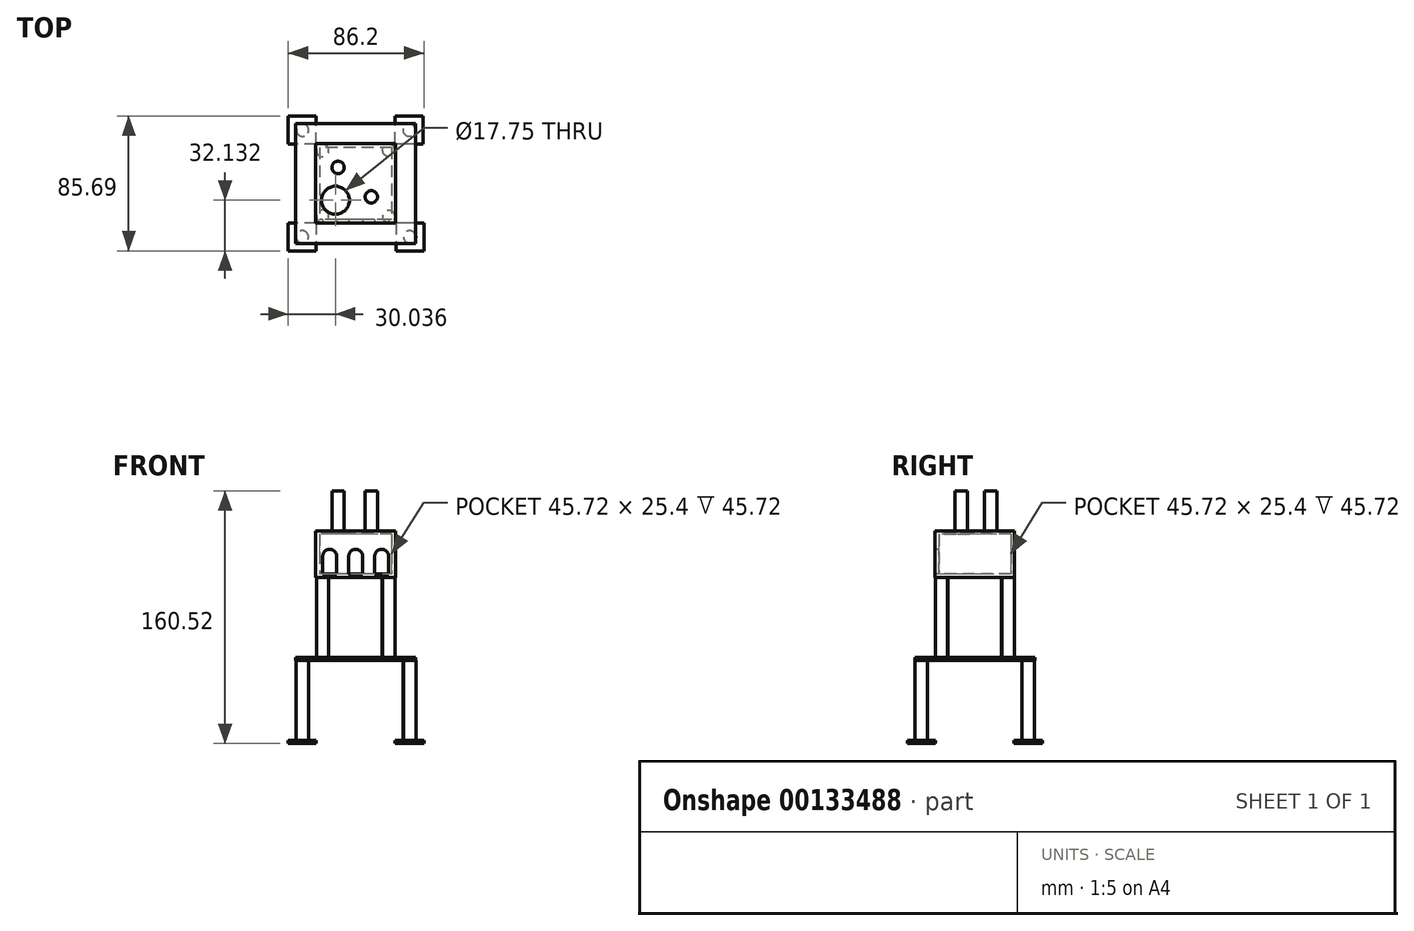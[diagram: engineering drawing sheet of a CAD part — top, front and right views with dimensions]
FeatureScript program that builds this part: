
annotation { "Feature Type Name" : "Feature", "Feature Type Description" : "" }
export const myFeature = defineFeature(function(context is Context, id is Id, definition is map)
    precondition{}
    {
        {
            var Q0;
            Q0=qCreatedBy(makeId("Top.planeOp"),FACE);
            var sketch = newSketch(context, id + "F0", { "sketchPlane" : qUnion([Q0])});
            skLineSegment(sketch, "E0.bottom", {"start": v(38.1, 38.1) * mm, "end": v(-38.1, 38.1) * mm});
            skLineSegment(sketch, "E0.top", {"start": v(38.1, -38.1) * mm, "end": v(-38.1, -38.1) * mm});
            skLineSegment(sketch, "E0.left", {"start": v(38.1, 38.1) * mm, "end": v(38.1, -38.1) * mm});
            skLineSegment(sketch, "E0.right", {"start": v(-38.1, 38.1) * mm, "end": v(-38.1, -38.1) * mm});
            skPoint(sketch, "E0.middle", {"position": v(0, 0) * mm});
            skSolve(sketch);
        }
        {
            var Q0;
            Q0=makeQuery(id+"F0.imprint","IMPRINT",FACE,{"disambiguationData":[TD([[makeQuery(id+"F0.imprint","IMPRINT",EDGE,{"derivedFrom":sQuery(id+"F0.wireOp",EDGE,"E0.bottom")}),1.0]])]});
            extrude(context, id + "F1", {"entities" : qUnion([Q0]), "oppositeDirection" : true, "depth" : 2.03 * mm});
        }
        {
            var Q0;
            Q0=makeQuery(id+"F1.opExtrude","CAP_FACE",FACE,{"disambiguationData":[OSD([sQuery(id+"F0.wireOp",EDGE,"E0.bottom"),sQuery(id+"F0.wireOp",EDGE,"E0.top"),sQuery(id+"F0.wireOp",EDGE,"E0.left"),sQuery(id+"F0.wireOp",EDGE,"E0.right")])],"isStart":true});
            var sketch = newSketch(context, id + "F2", { "sketchPlane" : qUnion([Q0])});
            skCircle(sketch, "E1", {"center": v(-21, -20.95) * mm, "radius": 3.94 * mm});
            skCircle(sketch, "E2", {"center": v(-21.04, 20.86) * mm, "radius": 3.94 * mm});
            skLineSegment(sketch, "E3.bottom", {"start": v(25.4, 25.4) * mm, "end": v(-25.4, 25.4) * mm, "construction": true});
            skLineSegment(sketch, "E3.top", {"start": v(25.4, -25.4) * mm, "end": v(-25.4, -25.4) * mm, "construction": true});
            skLineSegment(sketch, "E3.right", {"start": v(-25.4, 25.4) * mm, "end": v(-25.4, -25.4) * mm, "construction": true});
            skPoint(sketch, "E3.middle", {"position": v(0, 0) * mm});
            skLineSegment(sketch, "E4", {"start": v(25.4, 25.4) * mm, "end": v(25.4, -25.4) * mm, "construction": true});
            skCircle(sketch, "E5", {"center": v(21.05, -21.17) * mm, "radius": 3.94 * mm});
            skCircle(sketch, "E6", {"center": v(20.8, 21.17) * mm, "radius": 3.94 * mm});
            skSolve(sketch);
        }
        {
            var Q0;
            Q0 = qSketchRegion(id + "F2", true);
            extrude(context, id + "F3", {"entities" : qUnion([Q0]), "operationType" : NewBodyOperationType.ADD, "depth" : 50.8 * mm});
        }
        {
            var Q0;
            Q0=makeQuery(id+"F3.opExtrude","CAP_FACE",FACE,{"disambiguationData":[OSD([sQuery(id+"F2.wireOp",EDGE,"E2")])],"isStart":false});
            var sketch = newSketch(context, id + "F4", { "sketchPlane" : qUnion([Q0])});
            skLineSegment(sketch, "E7.bottom", {"start": v(-25.4, 25.16) * mm, "end": v(25.4, 25.16) * mm});
            skLineSegment(sketch, "E7.top", {"start": v(-25.4, -25.16) * mm, "end": v(25.4, -25.16) * mm});
            skLineSegment(sketch, "E7.left", {"start": v(-25.4, 25.16) * mm, "end": v(-25.4, -25.16) * mm});
            skLineSegment(sketch, "E7.right", {"start": v(25.4, 25.16) * mm, "end": v(25.4, -25.16) * mm});
            skPoint(sketch, "E7.middle", {"position": v(0, 0) * mm});
            skSolve(sketch);
        }
        {
            var Q0;
            Q0 = qSketchRegion(id + "F4", true);
            extrude(context, id + "F5", {"entities" : qUnion([Q0]), "operationType" : NewBodyOperationType.ADD, "depth" : 2.03 * mm});
        }
        {
            var Q0;
            Q0=makeQuery(id+"F5.opExtrude","CAP_FACE",FACE,{"disambiguationData":[OSD([sQuery(id+"F4.wireOp",EDGE,"E7.bottom"),sQuery(id+"F4.wireOp",EDGE,"E7.top"),sQuery(id+"F4.wireOp",EDGE,"E7.left"),sQuery(id+"F4.wireOp",EDGE,"E7.right")])],"isStart":false});
            var sketch = newSketch(context, id + "F6", { "sketchPlane" : qUnion([Q0])});
            skLineSegment(sketch, "E8.bottom", {"start": v(25.4, 25.16) * mm, "end": v(-25.4, 25.16) * mm});
            skLineSegment(sketch, "E8.top", {"start": v(25.4, -25.16) * mm, "end": v(-25.4, -25.16) * mm});
            skLineSegment(sketch, "E8.left", {"start": v(25.4, 25.16) * mm, "end": v(25.4, -25.16) * mm});
            skLineSegment(sketch, "E8.right", {"start": v(-25.4, 25.16) * mm, "end": v(-25.4, -25.16) * mm});
            skPoint(sketch, "E8.middle", {"position": v(0, 0) * mm});
            skLineSegment(sketch, "E9.bottom", {"start": v(22.86, 22.86) * mm, "end": v(-22.86, 22.86) * mm});
            skLineSegment(sketch, "E9.top", {"start": v(22.86, -22.86) * mm, "end": v(-22.86, -22.86) * mm});
            skLineSegment(sketch, "E9.left", {"start": v(22.86, 22.86) * mm, "end": v(22.86, -22.86) * mm});
            skLineSegment(sketch, "E9.right", {"start": v(-22.86, 22.86) * mm, "end": v(-22.86, -22.86) * mm});
            skSolve(sketch);
        }
        {
            var Q0;
            Q0=makeQuery(id+"F6.imprint","IMPRINT",FACE,{"disambiguationData":[TD([[makeQuery(id+"F6.imprint","IMPRINT",EDGE,{"derivedFrom":sQuery(id+"F6.wireOp",EDGE,"E8.bottom")}),-1.0]])]});
            extrude(context, id + "F7", {"entities" : qUnion([Q0]), "operationType" : NewBodyOperationType.ADD, "depth" : 25.4 * mm});
        }
        {
            var Q0;
            Q0=makeQuery(id+"F7.opExtrude","CAP_FACE",FACE,{"disambiguationData":[OSD([sQuery(id+"F6.wireOp",EDGE,"E8.bottom"),sQuery(id+"F6.wireOp",EDGE,"E8.top"),sQuery(id+"F6.wireOp",EDGE,"E8.left"),sQuery(id+"F6.wireOp",EDGE,"E8.right"),sQuery(id+"F6.wireOp",EDGE,"E9.bottom"),sQuery(id+"F6.wireOp",EDGE,"E9.top"),sQuery(id+"F6.wireOp",EDGE,"E9.left"),sQuery(id+"F6.wireOp",EDGE,"E9.right")])],"isStart":false});
            var sketch = newSketch(context, id + "F8", { "sketchPlane" : qUnion([Q0])});
            skLineSegment(sketch, "E10.bottom", {"start": v(25.4, 25.16) * mm, "end": v(-25.4, 25.16) * mm});
            skLineSegment(sketch, "E10.top", {"start": v(25.4, -25.16) * mm, "end": v(-25.4, -25.16) * mm});
            skLineSegment(sketch, "E10.left", {"start": v(25.4, 25.16) * mm, "end": v(25.4, -25.16) * mm});
            skLineSegment(sketch, "E10.right", {"start": v(-25.4, 25.16) * mm, "end": v(-25.4, -25.16) * mm});
            skPoint(sketch, "E10.middle", {"position": v(0, 0) * mm});
            skCircle(sketch, "E11", {"center": v(-12.85, -10.73) * mm, "radius": 8.87 * mm});
            skSolve(sketch);
        }
        {
            var Q0;
            Q0=makeQuery(id+"F8.imprint","IMPRINT",FACE,{"disambiguationData":[TD([[makeQuery(id+"F8.imprint","IMPRINT",EDGE,{"derivedFrom":sQuery(id+"F8.wireOp",EDGE,"E11")}),-1.0]])]});
            var Q1;
            Q1=makeQuery(id+"F8.imprint","IMPRINT",FACE,{"disambiguationData":[TD([[makeQuery(id+"F8.imprint","IMPRINT",EDGE,{"derivedFrom":sQuery(id+"F8.wireOp",EDGE,"E10.bottom")}),-1.0]])]});
            extrude(context, id + "F9", {"entities" : qUnion([Q0, Q1]), "operationType" : NewBodyOperationType.ADD, "depth" : 2.03 * mm});
        }
        {
            var Q0;
            Q0=makeQuery(id+"F9.boolean.opBoolean","MERGE",FACE,{"derivedFrom":[makeQuery(id+"F7.boolean.opBoolean","MERGE",FACE,{"derivedFrom":[makeQuery(id+"F5.opExtrude","SWEPT_FACE",FACE,{"disambiguationData":[OSD([sQuery(id+"F4.wireOp",EDGE,"E7.top")])]}),makeQuery(id+"F7.opExtrude","SWEPT_FACE",FACE,{"disambiguationData":[OSD([sQuery(id+"F6.wireOp",EDGE,"E8.top")])]})]}),makeQuery(id+"F9.opExtrude","SWEPT_FACE",FACE,{"disambiguationData":[OSD([sQuery(id+"F8.wireOp",EDGE,"E10.top")])]})]});
            var sketch = newSketch(context, id + "F10", { "sketchPlane" : qUnion([Q0])});
            skLineSegment(sketch, "E12.bottom", {"start": v(-20.96, 50.8) * mm, "end": v(-12.06, 50.8) * mm});
            skLineSegment(sketch, "E12.top", {"start": v(-20.96, 64.09) * mm, "end": v(-12.07, 64.09) * mm});
            skLineSegment(sketch, "E12.left", {"start": v(-20.96, 50.8) * mm, "end": v(-20.96, 64.09) * mm});
            skLineSegment(sketch, "E12.right", {"start": v(-12.06, 50.8) * mm, "end": v(-12.07, 64.09) * mm});
            skLineSegment(sketch, "E13.bottom", {"start": v(-4.45, 50.8) * mm, "end": v(4.44, 50.8) * mm});
            skLineSegment(sketch, "E13.top", {"start": v(-4.45, 64.09) * mm, "end": v(4.44, 64.09) * mm});
            skLineSegment(sketch, "E13.left", {"start": v(-4.45, 50.8) * mm, "end": v(-4.45, 64.09) * mm});
            skLineSegment(sketch, "E13.right", {"start": v(4.44, 50.8) * mm, "end": v(4.44, 64.09) * mm});
            skLineSegment(sketch, "E14.bottom", {"start": v(12.06, 50.8) * mm, "end": v(20.95, 50.8) * mm});
            skLineSegment(sketch, "E14.top", {"start": v(12.06, 64.09) * mm, "end": v(20.95, 64.09) * mm});
            skLineSegment(sketch, "E14.left", {"start": v(12.06, 50.8) * mm, "end": v(12.06, 64.09) * mm});
            skLineSegment(sketch, "E14.right", {"start": v(20.95, 50.8) * mm, "end": v(20.95, 64.09) * mm});
            skArc(sketch, "E15", {"start": v(-12.07, 64.09) * mm, "mid": v(-16.51, 68.53) * mm, "end": v(-20.96, 64.09) * mm});
            skArc(sketch, "E16", {"start": v(4.44, 64.09) * mm, "mid": v(0, 68.53) * mm, "end": v(-4.45, 64.09) * mm});
            skArc(sketch, "E17", {"start": v(20.95, 64.09) * mm, "mid": v(16.5, 68.53) * mm, "end": v(12.06, 64.09) * mm});
            skLineSegment(sketch, "E18", {"start": v(-20.96, 52.83) * mm, "end": v(20.96, 52.83) * mm});
            skSolve(sketch);
        }
        {
            var Q0;
            {var subQ0=sQuery(id+"F10.wireOp",EDGE,"E14.top");Q0=makeQuery(id+"F10.imprint","IMPRINT",FACE,{"disambiguationData":[TD([[makeQuery(id+"F10.imprint","IMPRINT",EDGE,{"derivedFrom":subQ0}),-1.0]])]});}
            var Q1;
            Q1=makeQuery(id+"F10.imprint","IMPRINT",FACE,{"disambiguationData":[TD([[makeQuery(id+"F10.imprint","IMPRINT",EDGE,{"derivedFrom":sQuery(id+"F10.wireOp",EDGE,"E14.top")}),1.0]])]});
            var Q2;
            {var subQ0=sQuery(id+"F10.wireOp",EDGE,"E13.top");Q2=makeQuery(id+"F10.imprint","IMPRINT",FACE,{"disambiguationData":[TD([[makeQuery(id+"F10.imprint","IMPRINT",EDGE,{"derivedFrom":subQ0}),-1.0]])]});}
            var Q3;
            Q3=makeQuery(id+"F10.imprint","IMPRINT",FACE,{"disambiguationData":[TD([[makeQuery(id+"F10.imprint","IMPRINT",EDGE,{"derivedFrom":sQuery(id+"F10.wireOp",EDGE,"E13.top")}),1.0]])]});
            var Q4;
            {var subQ0=sQuery(id+"F10.wireOp",EDGE,"E12.top");Q4=makeQuery(id+"F10.imprint","IMPRINT",FACE,{"disambiguationData":[TD([[makeQuery(id+"F10.imprint","IMPRINT",EDGE,{"derivedFrom":subQ0}),-1.0]])]});}
            var Q5;
            Q5=makeQuery(id+"F10.imprint","IMPRINT",FACE,{"disambiguationData":[TD([[makeQuery(id+"F10.imprint","IMPRINT",EDGE,{"derivedFrom":sQuery(id+"F10.wireOp",EDGE,"E12.top")}),1.0]])]});
            extrude(context, id + "F11", {"entities" : qUnion([Q0, Q1, Q2, Q3, Q4, Q5]), "operationType" : NewBodyOperationType.REMOVE, "oppositeDirection" : true, "depth" : 7.62 * mm});
        }
        {
            var Q0;
            Q0=makeQuery(id+"F1.opExtrude","CAP_FACE",FACE,{"disambiguationData":[OSD([sQuery(id+"F0.wireOp",EDGE,"E0.bottom"),sQuery(id+"F0.wireOp",EDGE,"E0.top"),sQuery(id+"F0.wireOp",EDGE,"E0.left"),sQuery(id+"F0.wireOp",EDGE,"E0.right")])],"isStart":false});
            var sketch = newSketch(context, id + "F12", { "sketchPlane" : qUnion([Q0])});
            skCircle(sketch, "E19", {"center": v(-34, 33.97) * mm, "radius": 3.94 * mm});
            skCircle(sketch, "E20", {"center": v(34.26, 33.98) * mm, "radius": 3.94 * mm});
            skCircle(sketch, "E21", {"center": v(-33.8, -33.75) * mm, "radius": 3.94 * mm});
            skCircle(sketch, "E22", {"center": v(33.93, -33.9) * mm, "radius": 3.94 * mm});
            skSolve(sketch);
        }
        {
            var Q0;
            Q0 = qSketchRegion(id + "F12", true);
            extrude(context, id + "F13", {"entities" : qUnion([Q0]), "operationType" : NewBodyOperationType.ADD, "depth" : 50.8 * mm});
        }
        {
            var Q0;
            Q0=makeQuery(id+"F13.opExtrude","CAP_FACE",FACE,{"disambiguationData":[OSD([sQuery(id+"F12.wireOp",EDGE,"E19")])],"isStart":false});
            var sketch = newSketch(context, id + "F14", { "sketchPlane" : qUnion([Q0])});
            skLineSegment(sketch, "E23.bottom", {"start": v(-25.1, 25.08) * mm, "end": v(-42.89, 25.08) * mm});
            skLineSegment(sketch, "E23.top", {"start": v(-25.1, 42.86) * mm, "end": v(-42.89, 42.86) * mm});
            skLineSegment(sketch, "E23.left", {"start": v(-25.1, 25.08) * mm, "end": v(-25.1, 42.86) * mm});
            skLineSegment(sketch, "E23.right", {"start": v(-42.89, 25.08) * mm, "end": v(-42.89, 42.86) * mm});
            skPoint(sketch, "E23.middle", {"position": v(-34, 33.97) * mm});
            skLineSegment(sketch, "E24.bottom", {"start": v(43.31, 25.08) * mm, "end": v(25.53, 25.08) * mm});
            skLineSegment(sketch, "E24.top", {"start": v(43.31, 42.86) * mm, "end": v(25.53, 42.86) * mm});
            skLineSegment(sketch, "E24.left", {"start": v(43.31, 25.08) * mm, "end": v(43.31, 42.86) * mm});
            skLineSegment(sketch, "E24.right", {"start": v(25.53, 25.08) * mm, "end": v(25.53, 42.86) * mm});
            skPoint(sketch, "E24.middle", {"position": v(34.42, 33.97) * mm});
            skLineSegment(sketch, "E25.bottom", {"start": v(-25.03, -24.86) * mm, "end": v(-42.81, -24.86) * mm});
            skLineSegment(sketch, "E25.top", {"start": v(-25.03, -42.64) * mm, "end": v(-42.81, -42.64) * mm});
            skLineSegment(sketch, "E25.left", {"start": v(-25.03, -24.86) * mm, "end": v(-25.03, -42.64) * mm});
            skLineSegment(sketch, "E25.right", {"start": v(-42.81, -24.86) * mm, "end": v(-42.81, -42.64) * mm});
            skPoint(sketch, "E25.middle", {"position": v(-33.92, -33.75) * mm});
            skLineSegment(sketch, "E26.bottom", {"start": v(42.74, -25.05) * mm, "end": v(24.96, -25.05) * mm});
            skLineSegment(sketch, "E26.top", {"start": v(42.74, -42.83) * mm, "end": v(24.96, -42.83) * mm});
            skLineSegment(sketch, "E26.left", {"start": v(42.74, -25.05) * mm, "end": v(42.74, -42.83) * mm});
            skLineSegment(sketch, "E26.right", {"start": v(24.96, -25.05) * mm, "end": v(24.96, -42.83) * mm});
            skPoint(sketch, "E26.middle", {"position": v(33.85, -33.94) * mm});
            skSolve(sketch);
        }
        {
            var Q0;
            Q0 = qSketchRegion(id + "F14", true);
            extrude(context, id + "F15", {"entities" : qUnion([Q0]), "operationType" : NewBodyOperationType.ADD, "depth" : 2.03 * mm});
        }
        {
            var Q0;
            Q0=makeQuery(id+"F9.opExtrude","CAP_FACE",FACE,{"disambiguationData":[OSD([sQuery(id+"F8.wireOp",EDGE,"E10.bottom"),sQuery(id+"F8.wireOp",EDGE,"E10.top"),sQuery(id+"F8.wireOp",EDGE,"E10.left"),sQuery(id+"F8.wireOp",EDGE,"E10.right"),sQuery(id+"F8.wireOp",EDGE,"E11")])],"isStart":false});
            var sketch = newSketch(context, id + "F16", { "sketchPlane" : qUnion([Q0])});
            skCircle(sketch, "E27", {"center": v(-11.22, 10.1) * mm, "radius": 3.94 * mm});
            skCircle(sketch, "E28", {"center": v(9.89, -8.6) * mm, "radius": 3.94 * mm});
            skSolve(sketch);
        }
        {
            var Q0;
            Q0 = qSketchRegion(id + "F16", true);
            extrude(context, id + "F17", {"entities" : qUnion([Q0]), "operationType" : NewBodyOperationType.ADD, "depth" : 25.4 * mm});
        }
    });
